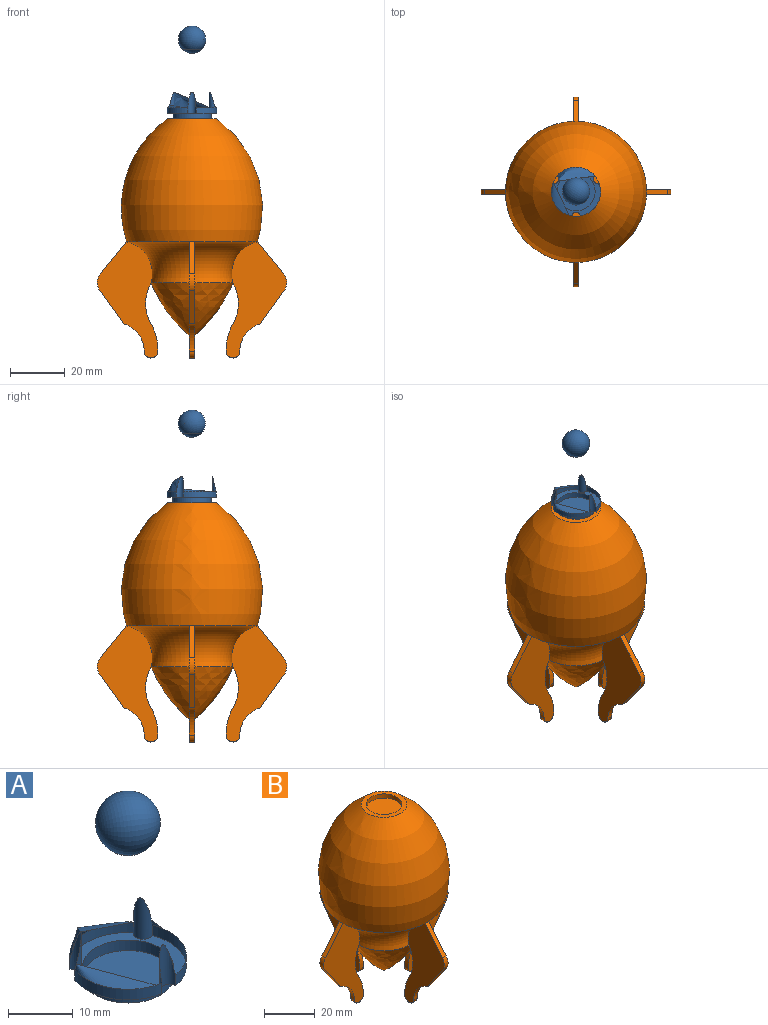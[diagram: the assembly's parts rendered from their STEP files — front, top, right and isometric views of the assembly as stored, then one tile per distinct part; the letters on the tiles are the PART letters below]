
ASSEMBLY  parts=2 mates=1
PART A: 15 faces, bbox 18x18x31.5 mm
  f0: cylinder r=9mm len=12.02mm, axis (0,0,-1), area 31.7mm2, adj f1,f2,f3,f4
  f1: plane 18x17.88mm, normal (0,0,-1), area 90.3mm2, adj f0,f2,f4,f5,f6,f7,f8
  f2: cylinder r=1.5mm len=7.77mm, axis (0,0,-1), area 25.1mm2, adj f0,f1,f3,f8
  f3: cone r=9mm half-angle=14.6deg, axis (0,0,-1), area 821.8mm2, adj f0,f2,f4,f6,f7,f8,f9
  f4: cylinder r=1.5mm len=7.77mm, axis (0,0,-1), area 25.1mm2, adj f0,f1,f3,f6
  f5: cylinder r=7mm len=14mm, axis (0,0,-1), area 88mm2, adj f1,f10
  f6: cylinder r=9mm len=12.02mm, axis (0,0,-1), area 31.7mm2, adj f1,f3,f4,f7
  f7: cylinder r=1.5mm len=7.77mm, axis (0,0,-1), area 25.1mm2, adj f1,f3,f6,f8
  f8: cylinder r=9mm len=13.88mm, axis (0,0,-1), area 31.7mm2, adj f1,f2,f3,f7
  f9: torus R=0.04mm, axis (-0.84,0.54,0), area 43.4mm2, adj f3
  f10: plane 14x14mm, normal (0,0,-1), area 153.9mm2, adj f5
  f11: torus R=0.04mm, axis (-0.84,0.54,0), area 309.9mm2
  f12: torus R=0.04mm, axis (-0.84,0.54,0), area 41.8mm2, adj f13,f14
  f13: cone r=9mm half-angle=14.6deg, axis (0,0,-1), area 1.5mm2, adj f12,f14
  f14: plane 5x5mm, normal (0,0,1), area 19.6mm2, adj f12,f13
PART B: 57 faces, bbox 69.3x69.3x87.5 mm
  f0: torus R=26.54mm, axis (0,0,-1), area 491.5mm2, adj f1,f51,f55,f56
  f1: plane 42.5x22.15mm, normal (1,0,0), area 483.9mm2, adj f0,f2,f43,f44,f45,f46,f47,f48
  f2: plane 2x0.02mm, normal (0,0.86,-0.51), area 0mm2, adj f1,f3,f4,f43,f50
  f3: plane 1x0.02mm, normal (0,0,1), area 0mm2, adj f2,f4,f51
  f4: plane 42.5x22.15mm, normal (-1,0,0), area 483.9mm2, adj f2,f3,f5,f43,f44,f45,f46,f47
  f5: torus R=26.54mm, axis (0,0,-1), area 491.5mm2, adj f4,f6,f51,f56
  f6: plane 42.5x22.15mm, normal (0,1,0), area 483.9mm2, adj f5,f7,f35,f36,f37,f38,f39,f40
  f7: plane 2x0.02mm, normal (-0.86,0,-0.51), area 0mm2, adj f6,f8,f9,f35,f42
  f8: plane 1x0.02mm, normal (0,0,1), area 0mm2, adj f7,f9,f51
  f9: plane 42.5x22.15mm, normal (0,-1,0), area 483.9mm2, adj f7,f8,f10,f35,f36,f37,f38,f39
  f10: torus R=26.54mm, axis (0,0,-1), area 491.5mm2, adj f9,f11,f51,f56
  f11: plane 42.5x22.15mm, normal (-1,0,0), area 483.9mm2, adj f10,f12,f27,f28,f29,f30,f31,f32
  f12: plane 2x0.02mm, normal (0,-0.86,-0.51), area 0mm2, adj f11,f13,f14,f27,f34
  f13: plane 1x0.02mm, normal (0,0,1), area 0mm2, adj f12,f14,f51
  f14: plane 42.5x22.15mm, normal (1,0,0), area 483.9mm2, adj f12,f13,f15,f27,f28,f29,f30,f31
  f15: torus R=26.54mm, axis (0,0,-1), area 491.5mm2, adj f14,f16,f51,f56
  f16: plane 42.5x22.15mm, normal (0,-1,0), area 483.9mm2, adj f15,f17,f19,f20,f21,f22,f23,f24
  f17: plane 2x0.02mm, normal (0.86,0,-0.51), area 0mm2, adj f16,f18,f19,f26,f55
  f18: plane 1x0.02mm, normal (0,0,1), area 0mm2, adj f17,f51,f55
  f19: plane 11.74x9.64mm, normal (0.77,0,0.63), area 30.4mm2, adj f16,f17,f20,f55
  f20: cylinder r=5mm len=6.08mm, axis (0,-1,0), area 13.1mm2, adj f16,f19,f21,f55
  f21: plane 12.16x8.71mm, normal (0.81,0,-0.58), area 29.9mm2, adj f16,f20,f22,f55
  f22: cylinder r=10.42mm len=10mm, axis (0,-1,0), area 26.8mm2, adj f16,f21,f23,f55
  f23: cylinder r=2.5mm len=5mm, axis (0,-1,0), area 15.7mm2, adj f16,f22,f24,f55
  f24: cylinder r=18.89mm len=10mm, axis (0,-1,0), area 20.9mm2, adj f16,f23,f25,f55
  f25: cylinder r=15mm len=15mm, axis (0,-1,0), area 31.4mm2, adj f16,f24,f55,f56
  f26: plane 1x0.02mm, normal (0,0,1), area 0mm2, adj f16,f17,f51
  f27: plane 11.74x9.64mm, normal (0,-0.77,0.63), area 30.4mm2, adj f11,f12,f14,f28
  f28: cylinder r=5mm len=6.08mm, axis (-1,0,0), area 13.1mm2, adj f11,f14,f27,f29
  f29: plane 12.16x8.71mm, normal (0,-0.81,-0.58), area 29.9mm2, adj f11,f14,f28,f30
  f30: cylinder r=10.42mm len=10mm, axis (-1,0,0), area 26.8mm2, adj f11,f14,f29,f31
  f31: cylinder r=2.5mm len=5mm, axis (-1,0,0), area 15.7mm2, adj f11,f14,f30,f32
  f32: cylinder r=18.89mm len=10mm, axis (-1,0,0), area 20.9mm2, adj f11,f14,f31,f33
  f33: cylinder r=15mm len=15mm, axis (-1,0,0), area 31.4mm2, adj f11,f14,f32,f56
  f34: plane 1x0.02mm, normal (0,0,1), area 0mm2, adj f11,f12,f51
  f35: plane 11.74x9.64mm, normal (-0.77,0,0.63), area 30.4mm2, adj f6,f7,f9,f36
  f36: cylinder r=5mm len=6.08mm, axis (0,1,0), area 13.1mm2, adj f6,f9,f35,f37
  f37: plane 12.16x8.71mm, normal (-0.81,0,-0.58), area 29.9mm2, adj f6,f9,f36,f38
  f38: cylinder r=10.42mm len=10mm, axis (0,1,0), area 26.8mm2, adj f6,f9,f37,f39
  f39: cylinder r=2.5mm len=5mm, axis (0,1,0), area 15.7mm2, adj f6,f9,f38,f40
  f40: cylinder r=18.89mm len=10mm, axis (0,1,0), area 20.9mm2, adj f6,f9,f39,f41
  f41: cylinder r=15mm len=15mm, axis (0,1,0), area 31.4mm2, adj f6,f9,f40,f56
  f42: plane 1x0.02mm, normal (0,0,1), area 0mm2, adj f6,f7,f51
  f43: plane 11.74x9.64mm, normal (0,0.77,0.63), area 30.4mm2, adj f1,f2,f4,f44
  f44: cylinder r=5mm len=6.08mm, axis (1,0,0), area 13.1mm2, adj f1,f4,f43,f45
  f45: plane 12.16x8.71mm, normal (0,0.81,-0.58), area 29.9mm2, adj f1,f4,f44,f46
  f46: cylinder r=10.42mm len=10mm, axis (1,0,0), area 26.8mm2, adj f1,f4,f45,f47
  f47: cylinder r=2.5mm len=5mm, axis (1,0,0), area 15.7mm2, adj f1,f4,f46,f48
  f48: cylinder r=18.89mm len=10mm, axis (1,0,0), area 20.9mm2, adj f1,f4,f47,f49
  f49: cylinder r=15mm len=15mm, axis (1,0,0), area 31.4mm2, adj f1,f4,f48,f56
  f50: plane 1x0.02mm, normal (0,0,1), area 0mm2, adj f1,f2,f51
  f51: revolved ~51.69x51.69mm, area 6797.7mm2, adj f0,f3,f5,f8,f10,f13,f15,f18
  f52: plane 18x18mm, normal (0,0,1), area 100.5mm2, adj f51,f53
  f53: cylinder r=7mm len=14mm, axis (0,0,-1), area 88mm2, adj f52,f54
  f54: plane 14x14mm, normal (0,0,1), area 153.9mm2, adj f53
  f55: plane 42.5x22.15mm, normal (0,1,0), area 483.9mm2, adj f0,f17,f18,f19,f20,f21,f22,f23
  f56: revolved ~29.96x29.96mm, area 0.1mm2, adj f0,f5,f10,f15,f25,f33,f41,f49
PLACE A t=(-20.27,-40.6,-9.89)mm
PLACE B t=(10.16,-40.6,-50.99)mm
MATE fastened A.f5 <-> B.f0  axis (0,0,-1) through (-20.27,-40.6,-9.89)mm
